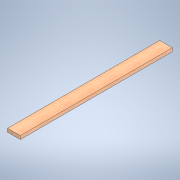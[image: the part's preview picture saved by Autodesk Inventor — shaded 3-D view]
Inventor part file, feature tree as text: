
AUTODESK INVENTOR PART (.ipt)
format: ipt  version: 2020.2 (Build 242310000, 310)  size: 101,376 bytes
history: native  units: in
note: dims shown in document units (in); Inventor stores cm internally (conversion verified against a paired STEP export)
features: extrude x1, sketch x1
ambient origin geometry x8: Origin, YZ Plane, XZ Plane, XY Plane, X Axis, Y Axis, Z Axis, Center Point
bodies: Solid1 (feature_tree)
feature tree (2):
  extrude  "Extrusion1"  Depth=1.5in
  sketch  "Sketch1"  dims[d0=5.5in d1=1.5in d3=0.0in]
